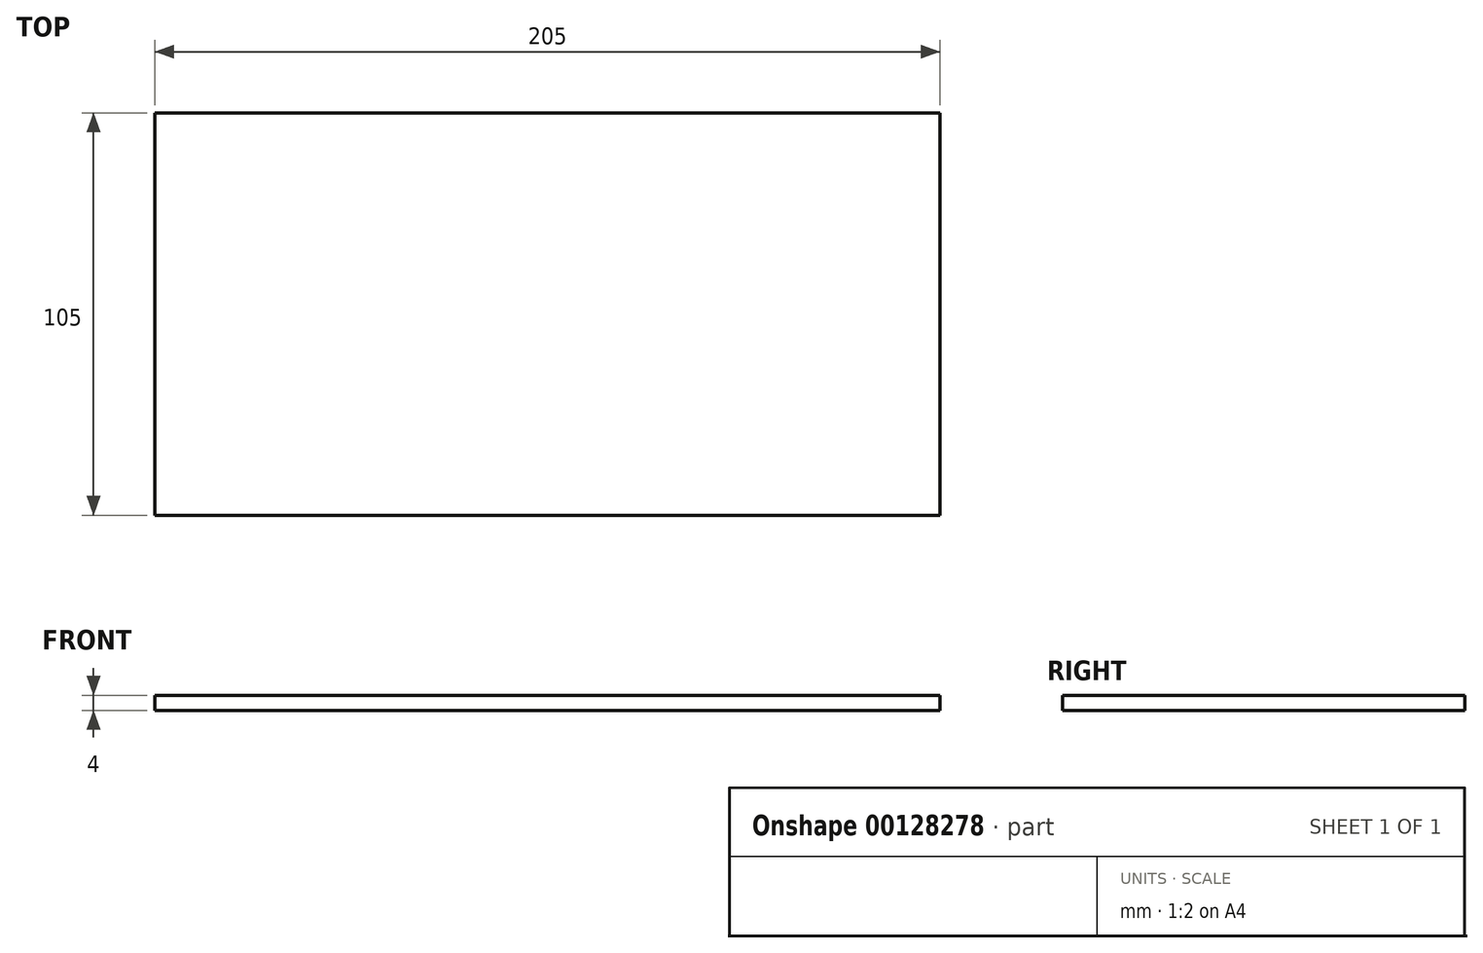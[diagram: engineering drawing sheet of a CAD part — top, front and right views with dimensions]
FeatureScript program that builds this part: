
annotation { "Feature Type Name" : "Feature", "Feature Type Description" : "" }
export const myFeature = defineFeature(function(context is Context, id is Id, definition is map)
    precondition{}
    {
        {
            var Q0;
            Q0=qCreatedBy(makeId("Top.planeOp"),FACE);
            var sketch = newSketch(context, id + "F0", { "sketchPlane" : qUnion([Q0])});
            skLineSegment(sketch, "E0.bottom", {"start": v(0, 0) * mm, "end": v(205, 0) * mm});
            skLineSegment(sketch, "E0.top", {"start": v(0, 105) * mm, "end": v(205, 105) * mm});
            skLineSegment(sketch, "E0.left", {"start": v(0, 0) * mm, "end": v(0, 105) * mm});
            skLineSegment(sketch, "E0.right", {"start": v(205, 0) * mm, "end": v(205, 105) * mm});
            skSolve(sketch);
        }
        {
            var Q0;
            Q0 = qSketchRegion(id + "F0", true);
            extrude(context, id + "F1", {"entities" : qUnion([Q0]), "depth" : 4 * mm});
        }
        {
            var Q0;
            Q0=qCreatedBy(makeId("Right.planeOp"),FACE);
            cPlane(context, id + "F2", {"entities" : qUnion([Q0]), "cplaneType" : CPlaneType.OFFSET, "offset" : 3 * mm, "width" : 150 * mm, "height" : 150 * mm});
        }
    });
